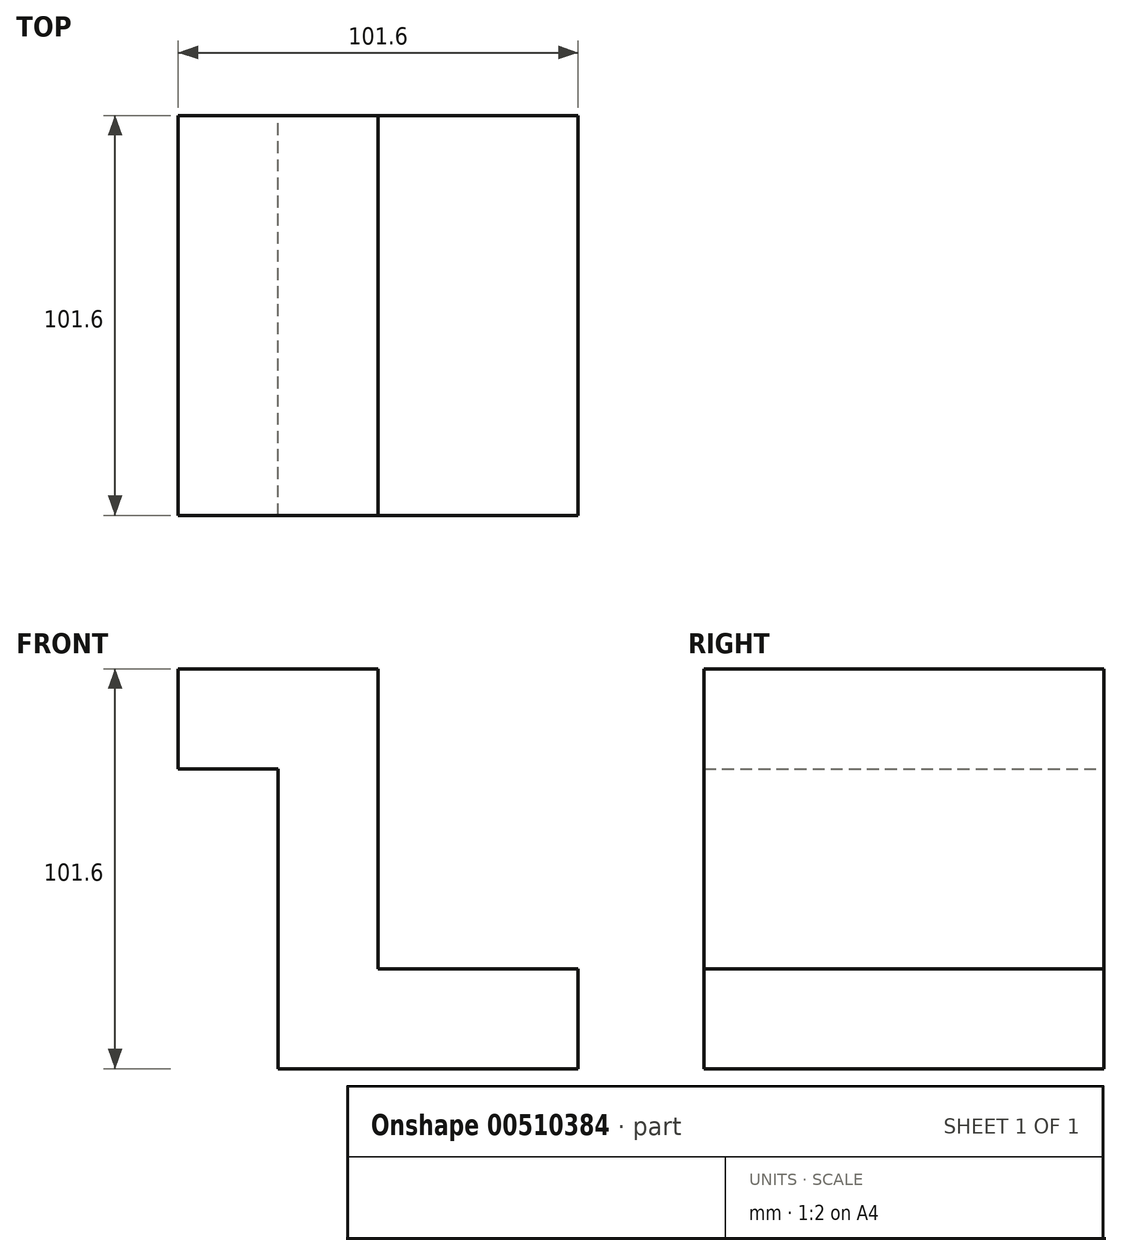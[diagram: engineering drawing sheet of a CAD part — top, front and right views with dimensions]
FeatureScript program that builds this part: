
annotation { "Feature Type Name" : "Feature", "Feature Type Description" : "" }
export const myFeature = defineFeature(function(context is Context, id is Id, definition is map)
    precondition{}
    {
        {
            var Q0;
            Q0=qCreatedBy(makeId("Front.planeOp"),FACE);
            var sketch = newSketch(context, id + "F0", { "sketchPlane" : qUnion([Q0])});
            skLineSegment(sketch, "E0", {"start": v(0, 0) * mm, "end": v(-76.2, 0) * mm});
            skLineSegment(sketch, "E1", {"start": v(-76.2, 0) * mm, "end": v(-76.2, 76.2) * mm});
            skLineSegment(sketch, "E2", {"start": v(-76.2, 76.2) * mm, "end": v(-101.6, 76.2) * mm});
            skLineSegment(sketch, "E3", {"start": v(-101.6, 76.2) * mm, "end": v(-101.6, 101.6) * mm});
            skLineSegment(sketch, "E4", {"start": v(-101.6, 101.6) * mm, "end": v(-50.8, 101.6) * mm});
            skLineSegment(sketch, "E5", {"start": v(-50.8, 101.6) * mm, "end": v(-50.8, 25.4) * mm});
            skLineSegment(sketch, "E6", {"start": v(-50.8, 25.4) * mm, "end": v(0, 25.4) * mm});
            skLineSegment(sketch, "E7", {"start": v(0, 25.4) * mm, "end": v(0, 0) * mm});
            skSolve(sketch);
        }
        {
            var Q0;
            Q0=makeQuery(id+"F0.imprint","IMPRINT",FACE,{"disambiguationData":[TD([[makeQuery(id+"F0.imprint","IMPRINT",EDGE,{"derivedFrom":sQuery(id+"F0.wireOp",EDGE,"E0")}),-1.0]])]});
            extrude(context, id + "F1", {"entities" : qUnion([Q0]), "depth" : 101.6 * mm});
        }
    });
